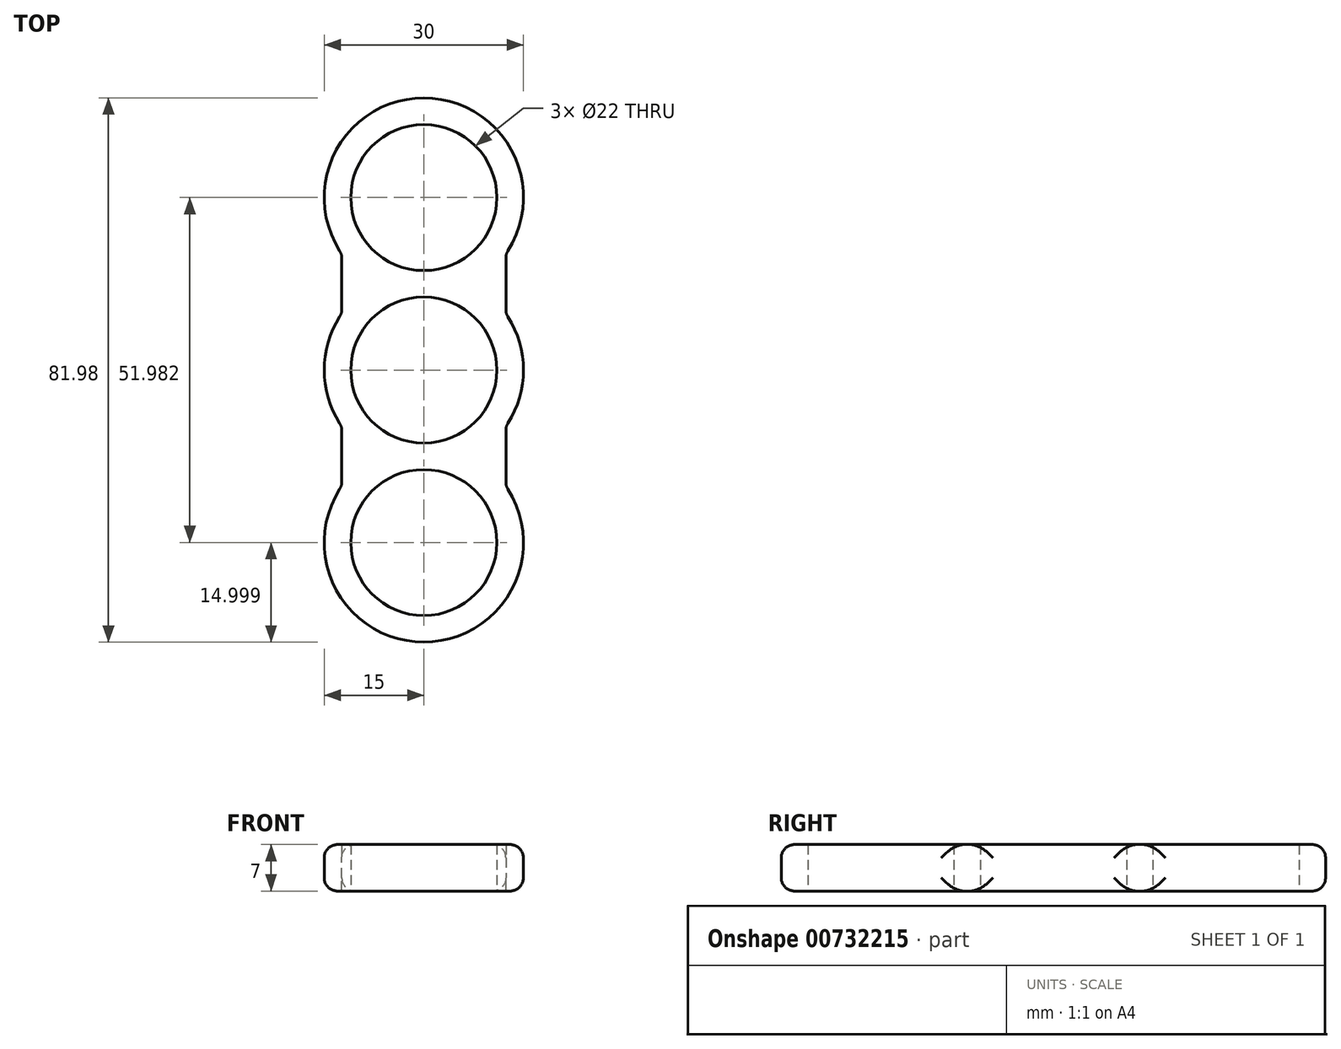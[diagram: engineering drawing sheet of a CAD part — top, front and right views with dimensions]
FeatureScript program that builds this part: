
annotation { "Feature Type Name" : "Feature", "Feature Type Description" : "" }
export const myFeature = defineFeature(function(context is Context, id is Id, definition is map)
    precondition{}
    {
        {
            var Q0;
            Q0=qCreatedBy(makeId("Top.planeOp"),FACE);
            var sketch = newSketch(context, id + "F0", { "sketchPlane" : qUnion([Q0])});
            skCircle(sketch, "E0", {"center": v(0, 0) * mm, "radius": 11 * mm});
            skCircle(sketch, "E1", {"center": v(0, 0) * mm, "radius": 15 * mm});
            skCircle(sketch, "E2", {"center": v(0, 26) * mm, "radius": 11 * mm});
            skCircle(sketch, "E3", {"center": v(0, 26) * mm, "radius": 15 * mm});
            skLineSegment(sketch, "E4", {"start": v(12.36, 17.49) * mm, "end": v(12.36, 8.5) * mm});
            skLineSegment(sketch, "E5.MirrorCS", {"start": v(-12.36, 17.49) * mm, "end": v(-12.36, 8.5) * mm});
            skLineSegment(sketch, "E6.MirrorCS", {"start": v(12.36, -17.49) * mm, "end": v(12.36, -8.5) * mm});
            skLineSegment(sketch, "E7.MirrorCS", {"start": v(-12.36, -17.49) * mm, "end": v(-12.36, -8.5) * mm});
            skCircle(sketch, "E8.MirrorC", {"center": v(0, -26) * mm, "radius": 15 * mm});
            skCircle(sketch, "E9.MirrorC", {"center": v(0, -26) * mm, "radius": 11 * mm});
            skSolve(sketch);
        }
        {
            var Q0;
            {var subQ0=sQuery(id+"F0.wireOp",EDGE,"E3");var subQ2=sQuery(id+"F0.wireOp",EDGE,"E1");var subQ7=makeQuery(id+"F0.imprint","INTERSECT",VERTEX,{"disambiguationData":[OD(0.0)],"derivedFrom":[subQ2,subQ0]});Q0=makeQuery(id+"F0.imprint","IMPRINT",FACE,{"disambiguationData":[TD([[makeQuery(id+"F0.imprint","IMPRINT",EDGE,{"disambiguationData":[TD([[subQ7,-1.0]])],"derivedFrom":subQ2}),-1.0]])]});}
            var Q1;
            {var subQ4=sQuery(id+"F0.wireOp",EDGE,"E3");var subQ7=sQuery(id+"F0.wireOp",EDGE,"E0");var subQ8=makeQuery(id+"F0.imprint","INTERSECT",VERTEX,{"disambiguationData":[OD(0.0)],"derivedFrom":[subQ7,subQ4]});Q1=makeQuery(id+"F0.imprint","IMPRINT",FACE,{"disambiguationData":[TD([[makeQuery(id+"F0.imprint","IMPRINT",EDGE,{"disambiguationData":[TD([[subQ8,1.0]])],"derivedFrom":subQ7}),-1.0]])]});}
            var Q2;
            {var subQ0=sQuery(id+"F0.wireOp",EDGE,"E4");Q2=makeQuery(id+"F0.imprint","IMPRINT",FACE,{"disambiguationData":[TD([[makeQuery(id+"F0.imprint","IMPRINT",EDGE,{"derivedFrom":subQ0}),-1.0]])]});}
            var Q3;
            {var subQ0=sQuery(id+"F0.wireOp",EDGE,"E5.MirrorCS");Q3=makeQuery(id+"F0.imprint","IMPRINT",FACE,{"disambiguationData":[TD([[makeQuery(id+"F0.imprint","IMPRINT",EDGE,{"derivedFrom":subQ0}),1.0]])]});}
            var Q4;
            {var subQ5=sQuery(id+"F0.wireOp",EDGE,"E3");var subQ7=sQuery(id+"F0.wireOp",EDGE,"E0");var subQ8=makeQuery(id+"F0.imprint","INTERSECT",VERTEX,{"disambiguationData":[OD(0.0)],"derivedFrom":[subQ7,subQ5]});Q4=makeQuery(id+"F0.imprint","IMPRINT",FACE,{"disambiguationData":[TD([[makeQuery(id+"F0.imprint","IMPRINT",EDGE,{"disambiguationData":[TD([[subQ8,-1.0]])],"derivedFrom":subQ7}),-1.0]])]});}
            var Q5;
            {var subQ0=sQuery(id+"F0.wireOp",EDGE,"E6.MirrorCS");Q5=makeQuery(id+"F0.imprint","IMPRINT",FACE,{"disambiguationData":[TD([[makeQuery(id+"F0.imprint","IMPRINT",EDGE,{"derivedFrom":subQ0}),1.0]])]});}
            var Q6;
            {var subQ0=sQuery(id+"F0.wireOp",EDGE,"E7.MirrorCS");Q6=makeQuery(id+"F0.imprint","IMPRINT",FACE,{"disambiguationData":[TD([[makeQuery(id+"F0.imprint","IMPRINT",EDGE,{"derivedFrom":subQ0}),-1.0]])]});}
            var Q7;
            {var subQ0=sQuery(id+"F0.wireOp",EDGE,"E8.MirrorC");var subQ1=sQuery(id+"F0.wireOp",EDGE,"E0");var subQ2=makeQuery(id+"F0.imprint","INTERSECT",VERTEX,{"disambiguationData":[OD(0.0)],"derivedFrom":[subQ1,subQ0]});Q7=makeQuery(id+"F0.imprint","IMPRINT",FACE,{"disambiguationData":[TD([[makeQuery(id+"F0.imprint","IMPRINT",EDGE,{"disambiguationData":[TD([[subQ2,-1.0]])],"derivedFrom":subQ1}),-1.0]])]});}
            var Q8;
            {var subQ0=sQuery(id+"F0.wireOp",EDGE,"E8.MirrorC");var subQ2=sQuery(id+"F0.wireOp",EDGE,"E1");var subQ5=makeQuery(id+"F0.imprint","INTERSECT",VERTEX,{"disambiguationData":[OD(0.0)],"derivedFrom":[subQ2,subQ0]});Q8=makeQuery(id+"F0.imprint","IMPRINT",FACE,{"disambiguationData":[TD([[makeQuery(id+"F0.imprint","IMPRINT",EDGE,{"disambiguationData":[TD([[subQ5,-1.0]])],"derivedFrom":subQ2}),-1.0]])]});}
            var Q9;
            {var subQ3=sQuery(id+"F0.wireOp",EDGE,"E3");var subQ7=sQuery(id+"F0.wireOp",EDGE,"E0");var subQ8=makeQuery(id+"F0.imprint","INTERSECT",VERTEX,{"disambiguationData":[OD(1.0)],"derivedFrom":[subQ7,subQ3]});Q9=makeQuery(id+"F0.imprint","IMPRINT",FACE,{"disambiguationData":[TD([[makeQuery(id+"F0.imprint","IMPRINT",EDGE,{"disambiguationData":[TD([[subQ8,1.0]])],"derivedFrom":subQ7}),-1.0]])]});}
            extrude(context, id + "F1", {"entities" : qUnion([Q0, Q1, Q2, Q3, Q4, Q5, Q6, Q7, Q8, Q9]), "depth" : 7 * mm, "offsetDistance" : 25 * mm});
        }
        {
            var Q0;
            Q0=makeQuery(id+"F1.opExtrude","SWEPT_FACE",FACE,{"disambiguationData":[OSD([sQuery(id+"F0.wireOp",EDGE,"E8.MirrorC")])]});
            var Q1;
            {var subQ0=sQuery(id+"F0.wireOp",EDGE,"E1");Q1=makeQuery(id+"F1.opExtrude","SWEPT_FACE",FACE,{"disambiguationData":[OSD([subQ0]),TDD([makeQuery(id+"F0.imprint","IMPRINT",EDGE,{"disambiguationData":[TD([[makeQuery(id+"F0.imprint","INTERSECT",VERTEX,{"derivedFrom":[subQ0,sQuery(id+"F0.wireOp",EDGE,"E4")]}),1.0]])],"derivedFrom":subQ0})])]});}
            var Q2;
            Q2=makeQuery(id+"F1.opExtrude","SWEPT_FACE",FACE,{"disambiguationData":[OSD([sQuery(id+"F0.wireOp",EDGE,"E3")])]});
            var Q3;
            {var subQ0=sQuery(id+"F0.wireOp",EDGE,"E1");Q3=makeQuery(id+"F1.opExtrude","SWEPT_FACE",FACE,{"disambiguationData":[OSD([subQ0]),TDD([makeQuery(id+"F0.imprint","IMPRINT",EDGE,{"disambiguationData":[TD([[makeQuery(id+"F0.imprint","INTERSECT",VERTEX,{"derivedFrom":[subQ0,sQuery(id+"F0.wireOp",EDGE,"E5.MirrorCS")]}),-1.0]])],"derivedFrom":subQ0})])]});}
            fillet(context, id + "F2", {"entities" : qUnion([Q0, Q1, Q2, Q3]), "radius" : 2 * mm, "tangentPropagation" : true, "allowEdgeOverflow" : false});
        }
    });
